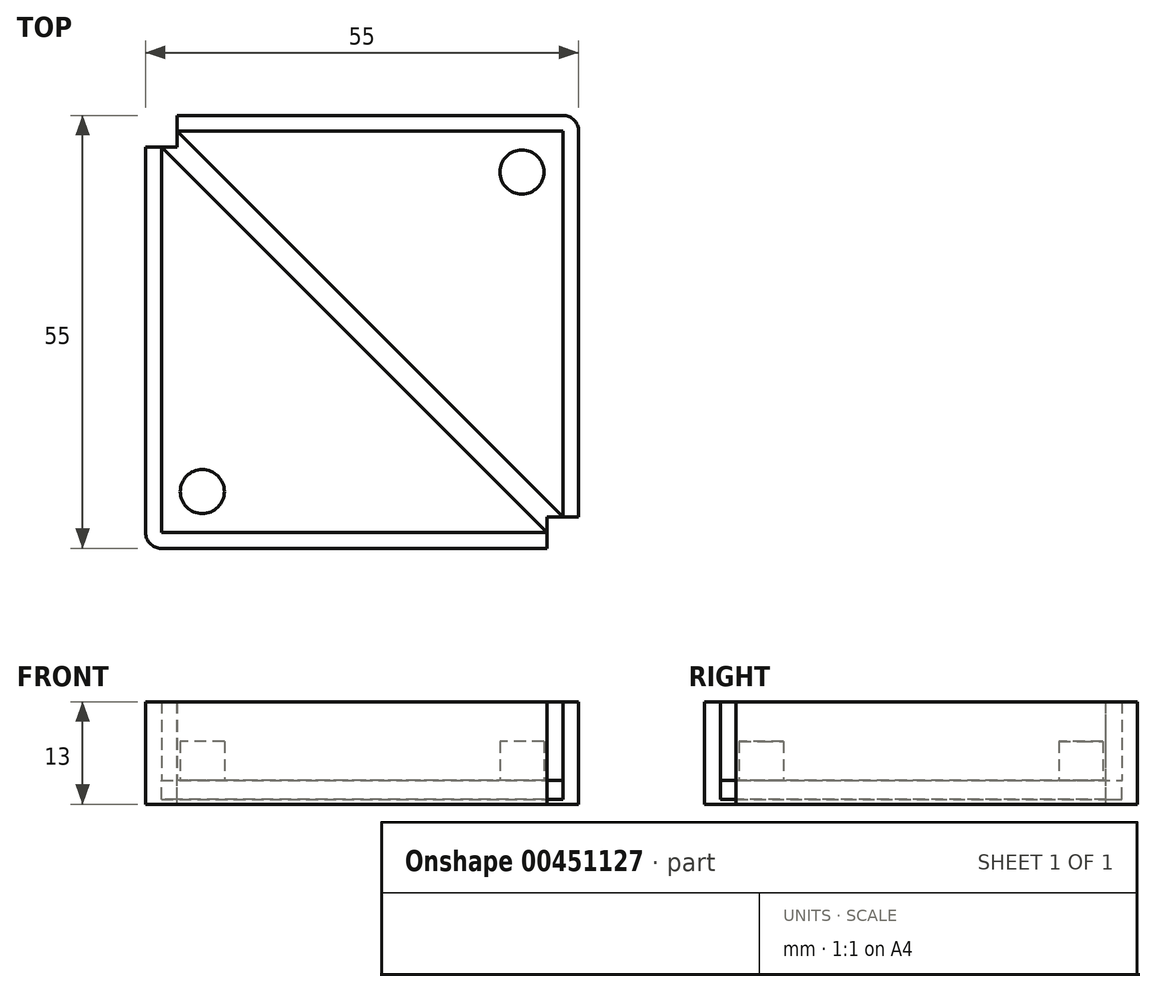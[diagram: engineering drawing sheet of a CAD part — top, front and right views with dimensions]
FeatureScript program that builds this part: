
annotation { "Feature Type Name" : "Feature", "Feature Type Description" : "" }
export const myFeature = defineFeature(function(context is Context, id is Id, definition is map)
    precondition{}
    {
        {
            var Q0;
            Q0=qCreatedBy(makeId("Top.planeOp"),FACE);
            var sketch = newSketch(context, id + "F0", { "sketchPlane" : qUnion([Q0])});
            skLineSegment(sketch, "E0.bottom", {"start": v(27.5, -27.5) * mm, "end": v(-27.5, -27.5) * mm});
            skLineSegment(sketch, "E0.top", {"start": v(27.5, 27.5) * mm, "end": v(-27.5, 27.5) * mm});
            skLineSegment(sketch, "E0.left", {"start": v(27.5, -27.5) * mm, "end": v(27.5, 27.5) * mm});
            skLineSegment(sketch, "E0.right", {"start": v(-27.5, -27.5) * mm, "end": v(-27.5, 27.5) * mm});
            skPoint(sketch, "E0.middle", {"position": v(0, 0) * mm});
            skSolve(sketch);
        }
        {
            var Q0;
            Q0 = qSketchRegion(id + "F0", true);
            extrude(context, id + "F1", {"entities" : qUnion([Q0]), "depth" : 3 * mm, "offsetDistance" : 25 * mm});
        }
        {
            var Q0;
            Q0=makeQuery(id+"F1.opExtrude","CAP_FACE",FACE,{"disambiguationData":[OSD([sQuery(id+"F0.wireOp",EDGE,"E0.bottom"),sQuery(id+"F0.wireOp",EDGE,"E0.top"),sQuery(id+"F0.wireOp",EDGE,"E0.left"),sQuery(id+"F0.wireOp",EDGE,"E0.right")])],"isStart":false});
            var sketch = newSketch(context, id + "F2", { "sketchPlane" : qUnion([Q0])});
            skLineSegment(sketch, "E1.bottom", {"start": v(27.5, -27.5) * mm, "end": v(-27.5, -27.5) * mm});
            skLineSegment(sketch, "E1.top", {"start": v(27.5, 27.5) * mm, "end": v(-27.5, 27.5) * mm});
            skLineSegment(sketch, "E1.left", {"start": v(27.5, -27.5) * mm, "end": v(27.5, 27.5) * mm});
            skLineSegment(sketch, "E1.right", {"start": v(-27.5, -27.5) * mm, "end": v(-27.5, 27.5) * mm});
            skPoint(sketch, "E1.middle", {"position": v(0, 0) * mm});
            skLineSegment(sketch, "E2.bottom", {"start": v(25.5, -25.5) * mm, "end": v(-25.5, -25.5) * mm});
            skLineSegment(sketch, "E2.top", {"start": v(25.5, 25.5) * mm, "end": v(-25.5, 25.5) * mm});
            skLineSegment(sketch, "E2.left", {"start": v(25.5, -25.5) * mm, "end": v(25.5, 25.5) * mm});
            skLineSegment(sketch, "E2.right", {"start": v(-25.5, -25.5) * mm, "end": v(-25.5, 25.5) * mm});
            skSolve(sketch);
        }
        {
            var Q0;
            Q0 = qSketchRegion(id + "F2", true);
            extrude(context, id + "F3", {"entities" : qUnion([Q0]), "operationType" : NewBodyOperationType.ADD, "depth" : 10 * mm, "offsetDistance" : 25 * mm});
        }
        {
            var Q0;
            Q0=makeQuery(id+"F1.opExtrude","CAP_FACE",FACE,{"disambiguationData":[OSD([sQuery(id+"F0.wireOp",EDGE,"E0.bottom"),sQuery(id+"F0.wireOp",EDGE,"E0.top"),sQuery(id+"F0.wireOp",EDGE,"E0.left"),sQuery(id+"F0.wireOp",EDGE,"E0.right")])],"isStart":false});
            var sketch = newSketch(context, id + "F4", { "sketchPlane" : qUnion([Q0])});
            skCircle(sketch, "E3", {"center": v(-20.3, -20.3) * mm, "radius": 2.8 * mm});
            skCircle(sketch, "E4", {"center": v(20.3, 20.3) * mm, "radius": 2.8 * mm});
            skSolve(sketch);
        }
        {
            var Q0;
            Q0 = qSketchRegion(id + "F4", true);
            extrude(context, id + "F5", {"entities" : qUnion([Q0]), "operationType" : NewBodyOperationType.ADD, "depth" : 5 * mm, "offsetDistance" : 25 * mm});
        }
        {
            var Q0;
            Q0=makeQuery(id+"F3.opExtrude","CAP_FACE",FACE,{"disambiguationData":[OSD([sQuery(id+"F2.wireOp",EDGE,"E1.bottom"),sQuery(id+"F2.wireOp",EDGE,"E1.top"),sQuery(id+"F2.wireOp",EDGE,"E1.left"),sQuery(id+"F2.wireOp",EDGE,"E1.right"),sQuery(id+"F2.wireOp",EDGE,"E2.bottom"),sQuery(id+"F2.wireOp",EDGE,"E2.top"),sQuery(id+"F2.wireOp",EDGE,"E2.left"),sQuery(id+"F2.wireOp",EDGE,"E2.right")])],"isStart":false});
            var sketch = newSketch(context, id + "F6", { "sketchPlane" : qUnion([Q0])});
            skLineSegment(sketch, "E5.bottom", {"start": v(-27.5, 27.5) * mm, "end": v(-23.5, 27.5) * mm});
            skLineSegment(sketch, "E5.top", {"start": v(-27.5, 23.5) * mm, "end": v(-23.5, 23.5) * mm});
            skLineSegment(sketch, "E5.left", {"start": v(-27.5, 27.5) * mm, "end": v(-27.5, 23.5) * mm});
            skLineSegment(sketch, "E5.right", {"start": v(-23.5, 27.5) * mm, "end": v(-23.5, 23.5) * mm});
            skLineSegment(sketch, "E6.bottom", {"start": v(27.5, -27.5) * mm, "end": v(23.5, -27.5) * mm});
            skLineSegment(sketch, "E6.top", {"start": v(27.5, -23.5) * mm, "end": v(23.5, -23.5) * mm});
            skLineSegment(sketch, "E6.left", {"start": v(27.5, -27.5) * mm, "end": v(27.5, -23.5) * mm});
            skLineSegment(sketch, "E6.right", {"start": v(23.5, -27.5) * mm, "end": v(23.5, -23.5) * mm});
            skSolve(sketch);
        }
        {
            var Q0;
            Q0 = qSketchRegion(id + "F6", true);
            extrude(context, id + "F7", {"entities" : qUnion([Q0]), "operationType" : NewBodyOperationType.REMOVE, "oppositeDirection" : true, "depth" : 25 * mm, "offsetDistance" : 25 * mm});
        }
        {
            var Q0;
            Q0=makeQuery(id+"F1.opExtrude","CAP_FACE",FACE,{"disambiguationData":[OSD([sQuery(id+"F0.wireOp",EDGE,"E0.bottom"),sQuery(id+"F0.wireOp",EDGE,"E0.top"),sQuery(id+"F0.wireOp",EDGE,"E0.left"),sQuery(id+"F0.wireOp",EDGE,"E0.right")])],"isStart":false});
            var sketch = newSketch(context, id + "F8", { "sketchPlane" : qUnion([Q0])});
            skLineSegment(sketch, "E7", {"start": v(-25.5, 23.5) * mm, "end": v(23.5, -25.5) * mm});
            skLineSegment(sketch, "E8", {"start": v(23.5, -25.5) * mm, "end": v(25.5, -23.5) * mm});
            skLineSegment(sketch, "E9", {"start": v(25.5, -23.5) * mm, "end": v(-23.5, 25.5) * mm});
            skLineSegment(sketch, "E10", {"start": v(-23.5, 25.5) * mm, "end": v(-25.5, 23.5) * mm});
            skSolve(sketch);
        }
        {
            var Q0;
            Q0 = qSketchRegion(id + "F8", true);
            extrude(context, id + "F9", {"entities" : qUnion([Q0]), "operationType" : NewBodyOperationType.REMOVE, "oppositeDirection" : true, "depth" : 2.4 * mm, "offsetDistance" : 25 * mm});
        }
        {
            var Q0;
            Q0=makeQuery(id+"F7.boolean.opBoolean","COPY",EDGE,{"derivedFrom":makeQuery(id+"F7.opExtrude","CAP_EDGE",EDGE,{"disambiguationData":[OSD([sQuery(id+"F6.wireOp",EDGE,"E5.top")])],"isStart":true})});
            var Q1;
            Q1=makeQuery(id+"F7.boolean.opBoolean","COPY",EDGE,{"derivedFrom":makeQuery(id+"F7.opExtrude","CAP_EDGE",EDGE,{"disambiguationData":[OSD([sQuery(id+"F6.wireOp",EDGE,"E6.right")])],"isStart":true})});
            var Q2;
            Q2=makeQuery(id+"F7.boolean.opBoolean","COPY",EDGE,{"derivedFrom":makeQuery(id+"F7.opExtrude","CAP_EDGE",EDGE,{"disambiguationData":[OSD([sQuery(id+"F6.wireOp",EDGE,"E6.top")])],"isStart":true})});
            var Q3;
            Q3=makeQuery(id+"F7.boolean.opBoolean","COPY",EDGE,{"derivedFrom":makeQuery(id+"F7.opExtrude","CAP_EDGE",EDGE,{"disambiguationData":[OSD([sQuery(id+"F6.wireOp",EDGE,"E5.right")])],"isStart":true})});
            var Q4;
            Q4=makeQuery(id+"F7.boolean.opBoolean","COPY",EDGE,{"derivedFrom":makeQuery(id+"F7.opExtrude","SWEPT_EDGE",EDGE,{"disambiguationData":[OSD([sQuery(id+"F2.wireOp",EDGE,"E1.right"),sQuery(id+"F6.wireOp",EDGE,"E5.top"),sQuery(id+"F6.wireOp",EDGE,"E5.left")])]})});
            var Q5;
            Q5=makeQuery(id+"F7.boolean.opBoolean","COPY",EDGE,{"derivedFrom":makeQuery(id+"F7.opExtrude","SWEPT_EDGE",EDGE,{"disambiguationData":[OSD([sQuery(id+"F2.wireOp",EDGE,"E1.top"),sQuery(id+"F6.wireOp",EDGE,"E5.bottom"),sQuery(id+"F6.wireOp",EDGE,"E5.right")])]})});
            var Q6;
            Q6=makeQuery(id+"F7.boolean.opBoolean","COPY",EDGE,{"derivedFrom":makeQuery(id+"F7.opExtrude","SWEPT_EDGE",EDGE,{"disambiguationData":[OSD([sQuery(id+"F2.wireOp",EDGE,"E1.bottom"),sQuery(id+"F6.wireOp",EDGE,"E6.bottom"),sQuery(id+"F6.wireOp",EDGE,"E6.right")])]})});
            var Q7;
            Q7=makeQuery(id+"F7.boolean.opBoolean","COPY",EDGE,{"derivedFrom":makeQuery(id+"F7.opExtrude","SWEPT_EDGE",EDGE,{"disambiguationData":[OSD([sQuery(id+"F2.wireOp",EDGE,"E1.left"),sQuery(id+"F6.wireOp",EDGE,"E6.top"),sQuery(id+"F6.wireOp",EDGE,"E6.left")])]})});
            var Q8;
            Q8=makeQuery(id+"F3.boolean.opBoolean","MERGE",EDGE,{"derivedFrom":[makeQuery(id+"F1.opExtrude","SWEPT_EDGE",EDGE,{"disambiguationData":[OSD([sQuery(id+"F0.wireOp",EDGE,"E0.bottom"),sQuery(id+"F0.wireOp",EDGE,"E0.right")])]}),makeQuery(id+"F3.opExtrude","SWEPT_EDGE",EDGE,{"disambiguationData":[OSD([sQuery(id+"F2.wireOp",EDGE,"E1.bottom"),sQuery(id+"F2.wireOp",EDGE,"E1.right")])]})]});
            var Q9;
            Q9=makeQuery(id+"F3.boolean.opBoolean","MERGE",EDGE,{"derivedFrom":[makeQuery(id+"F1.opExtrude","SWEPT_EDGE",EDGE,{"disambiguationData":[OSD([sQuery(id+"F0.wireOp",EDGE,"E0.top"),sQuery(id+"F0.wireOp",EDGE,"E0.left")])]}),makeQuery(id+"F3.opExtrude","SWEPT_EDGE",EDGE,{"disambiguationData":[OSD([sQuery(id+"F2.wireOp",EDGE,"E1.top"),sQuery(id+"F2.wireOp",EDGE,"E1.left")])]})]});
            fillet(context, id + "F10", {"entities" : qUnion([Q0, Q1, Q2, Q3, Q4, Q5, Q6, Q7, Q8, Q9]), "radius" : 2 * mm, "tangentPropagation" : true, "allowEdgeOverflow" : false});
        }
    });
